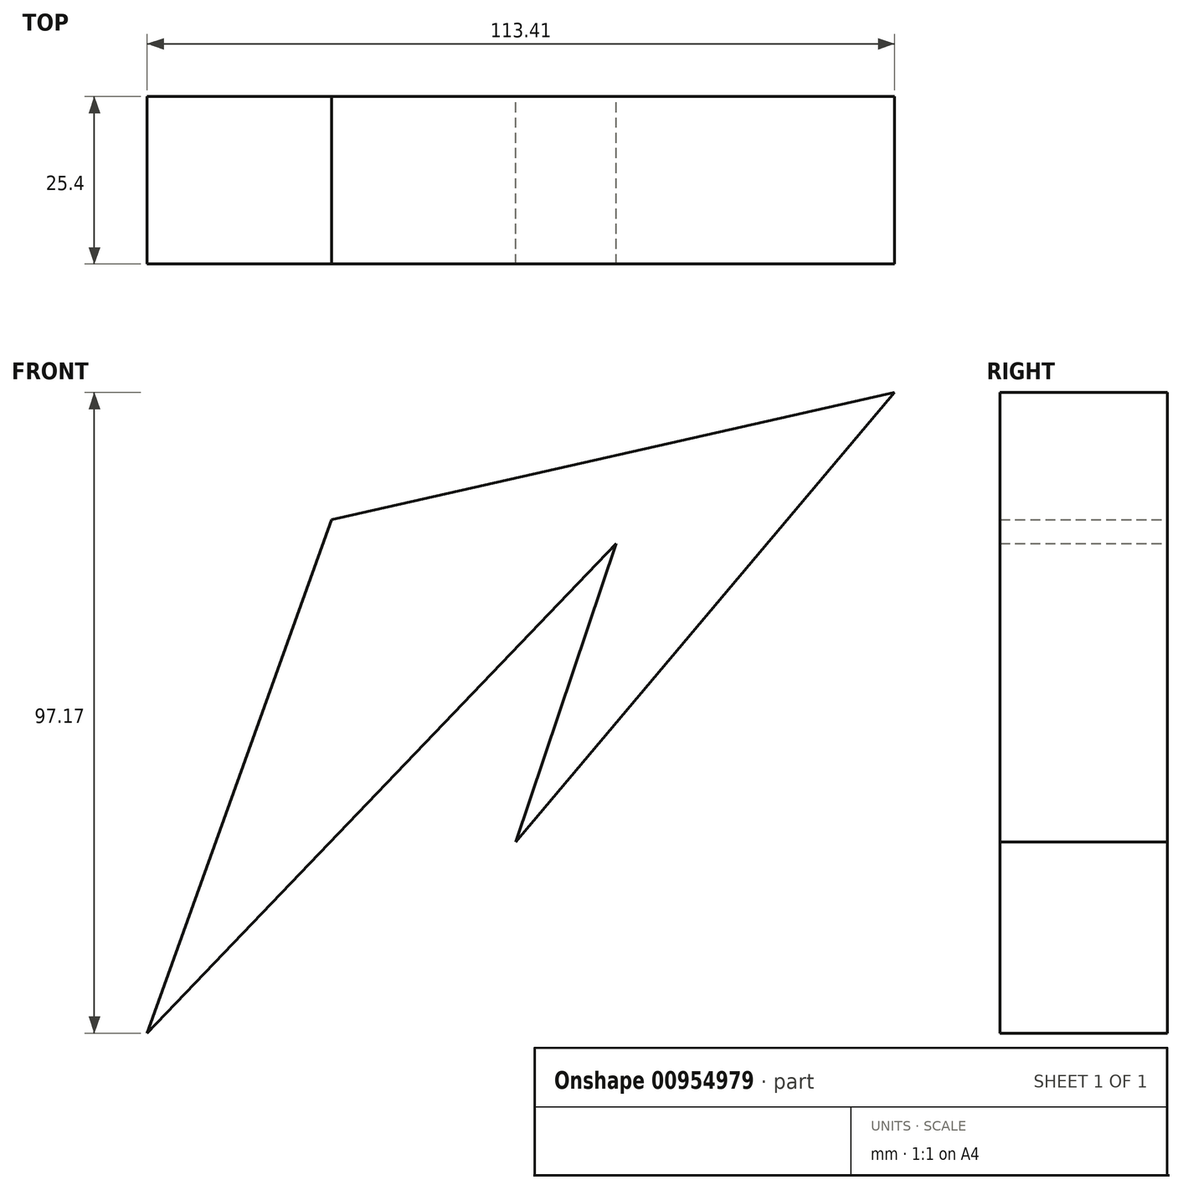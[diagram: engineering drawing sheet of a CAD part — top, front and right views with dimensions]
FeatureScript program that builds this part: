
annotation { "Feature Type Name" : "Feature", "Feature Type Description" : "" }
export const myFeature = defineFeature(function(context is Context, id is Id, definition is map)
    precondition{}
    {
        {
            var Q0;
            Q0=qCreatedBy(makeId("Front.planeOp"),FACE);
            var sketch = newSketch(context, id + "F0", { "sketchPlane" : qUnion([Q0])});
            skLineSegment(sketch, "E0", {"start": v(-79.38, -28.99) * mm, "end": v(-51.36, 48.9) * mm});
            skLineSegment(sketch, "E1", {"start": v(-51.36, 48.9) * mm, "end": v(34.03, 68.18) * mm});
            skLineSegment(sketch, "E2", {"start": v(34.03, 68.18) * mm, "end": v(-23.46, 0) * mm});
            skLineSegment(sketch, "E3", {"start": v(-23.46, 0) * mm, "end": v(-8.24, 45.27) * mm});
            skLineSegment(sketch, "E4", {"start": v(-8.24, 45.27) * mm, "end": v(-79.38, -28.99) * mm});
            skSolve(sketch);
        }
        {
            var Q0;
            Q0=makeQuery(id+"F0.imprint","IMPRINT",FACE,{"disambiguationData":[TD([[makeQuery(id+"F0.imprint","IMPRINT",EDGE,{"derivedFrom":sQuery(id+"F0.wireOp",EDGE,"E0")}),-1.0]])]});
            extrude(context, id + "F1", {"entities" : qUnion([Q0]), "depth" : 25.4 * mm, "offsetDistance" : 25.4 * mm});
        }
    });
